# Revit family: Reservoir_CESAME_3_6L_pneumatique
name_source: partatom
category: Plumbing Fixtures
units: mm (PartAtom-declared; Revit-internal decimal feet)

## family parameters
Always vertical = Yes
Cut with Voids When Loaded = No
OmniClass Number = 23.45.00.00
OmniClass Title = Sanitary, Laundry, and Cleaning Equipment
Part Type = Normal
Room Calculation Point = No
Round Connector Dimension = Use Diameter
Shared = No
Work Plane-Based = No

## types (1)
- Reservoir_CESAME_3_6L_pneumatique
    BIM object developer = www.concepsysbim.com
    BÂTI = NO
    BÂTI_Certification du produit = NF
    BÂTI_Graphique = MKT
    BÂTI_Hauteur maximum = 0 mm  [stored 0 ft]
    BÂTI_Hauteur minimum = 0 mm  [stored 0 ft]
    BÂTI_Largeur = 0 mm  [stored 0 ft]
    BÂTI_Longueur = 0 mm  [stored 0 ft]
    BÂTI_Marque = REGIPLAST
    BÂTI_Modèle = Réservoir à encastrer
    BÂTI_Modéle de Cuvette = Cuvettes suspendues
    BÂTI_Notice d'installation = https://professionnels.regiplast.fr
    BÂTI_Poids maximum = 400
    BÂTI_Produit = CESAME
    BÂTI_Règlage de la hauteur = 0 mm  [stored 0 ft]
    BÂTI_Référence = CE72
    BÂTI_Site internet/Page web = https://www.regiplast.fr
    BÂTI_Support vidéo = https://www.regiplast.fr
    BÂTI_Type d'actionnement = Pneumatique
    BÂTI_Type de mur = Habillage léger
    BÂTI_URL du produit = https://professionnels.regiplast.fr
    Description = pneumatique 3/6 litres
    Manufacturer = REGIPLAST
    Model = Réservoir à encastrer
    RACCORDEMENT EAU_Diamètre = 13 mm
    RACCORDEMENT EAU_Matériel du tube flexible = Acier inoxydable tressé
    RACCORDEMENT EAU_Position = TOP
    Regiplast_Matériel = <By Category>
    RÉSERVOIR = EST QUADRA V2 PN DD 6L CESAME REG
    RÉSERVOIR_Hauteur = 430 mm
    RÉSERVOIR_Largeur = 187 mm  [stored 0.613517 ft]
    RÉSERVOIR_Longueur = 185 mm  [stored 0.606955 ft]
    RÉSERVOIR_Matériel = PP
    RÉSERVOIR_Recharge = NO
    RÉSERVOIR_Volume de chasse = 6/3
    URL = https://professionnels.regiplast.fr
    USP = Vanne d'admission à ouverture retardée

note: [stored X ft] marks values corroborated as IEEE doubles in the binary element streams (Revit-internal decimal feet)

## geometry (parser evidence)
native form markers: Sweep x5
no freeform markers — native parametric forms only
